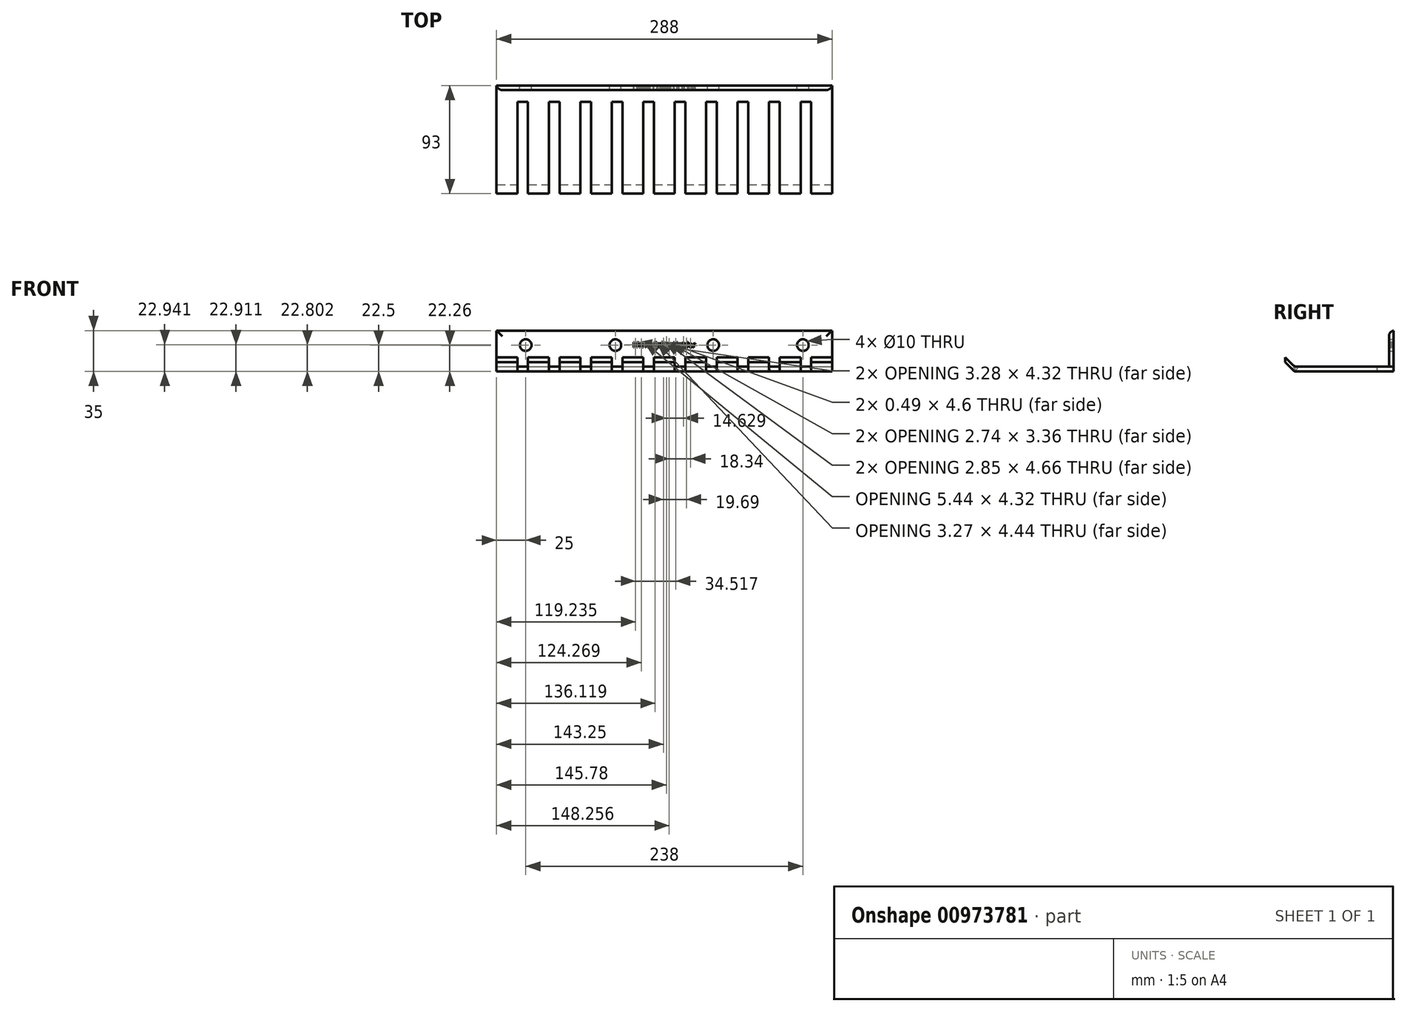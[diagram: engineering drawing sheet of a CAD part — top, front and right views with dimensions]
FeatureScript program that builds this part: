
annotation { "Feature Type Name" : "Feature", "Feature Type Description" : "" }
export const myFeature = defineFeature(function(context is Context, id is Id, definition is map)
    precondition{}
    {
        {
            var Q0;
            Q0=qCreatedBy(makeId("Front.planeOp"),FACE);
            var sketch = newSketch(context, id + "F0", { "sketchPlane" : qUnion([Q0])});
            skLineSegment(sketch, "E0", {"start": v(0, 0) * mm, "end": v(288, 0) * mm});
            skLineSegment(sketch, "E1", {"start": v(288, 0) * mm, "end": v(288, 35) * mm});
            skLineSegment(sketch, "E2", {"start": v(288, 35) * mm, "end": v(0, 35) * mm});
            skLineSegment(sketch, "E3", {"start": v(0, 35) * mm, "end": v(0, 0) * mm});
            skLineSegment(sketch, "E4", {"start": v(0, 22.5) * mm, "end": v(288, 22.5) * mm, "construction": true});
            skPoint(sketch, "E5", {"position": v(263, 22.5) * mm});
            skPoint(sketch, "E6", {"position": v(25, 22.5) * mm});
            skPoint(sketch, "E7", {"position": v(102, 22.5) * mm});
            skPoint(sketch, "E8", {"position": v(186, 22.5) * mm});
            skLineSegment(sketch, "E9", {"start": v(0, 4) * mm, "end": v(288, 4) * mm});
            skText(sketch, "E10", { "text": "HWM Cable Holder", "fontName": "OpenSans-Regular.ttf"});
            const initialGuessF0  = {"E10": [0.117, 0.02064, 1, 0, 0.00436]};
            skSetInitialGuess(sketch, initialGuessF0);
            skSolve(sketch);
        }
        {
            var Q0;
            {var subQ0=sQuery(id+"F0.wireOp",EDGE,"E2");Q0=makeQuery(id+"F0.imprint","IMPRINT",FACE,{"disambiguationData":[TD([[makeQuery(id+"F0.imprint","IMPRINT",EDGE,{"derivedFrom":subQ0}),1.0]])]});}
            extrude(context, id + "F1", {"entities" : qUnion([Q0]), "depth" : 4 * mm, "offsetDistance" : 25 * mm});
        }
        {
            var Q0;
            {var subQ0=sQuery(id+"F0.wireOp",EDGE,"E0");Q0=makeQuery(id+"F0.imprint","IMPRINT",FACE,{"disambiguationData":[TD([[makeQuery(id+"F0.imprint","IMPRINT",EDGE,{"derivedFrom":subQ0}),1.0]])]});}
            extrude(context, id + "F2", {"entities" : qUnion([Q0]), "depth" : 85 * mm, "offsetDistance" : 25 * mm});
        }
        {
            var Q0;
            Q0=sQuery(id+"F0.wireOp",VERTEX,"E6");
            var Q1;
            Q1=sQuery(id+"F0.wireOp",VERTEX,"E7");
            var Q2;
            Q2=sQuery(id+"F0.wireOp",VERTEX,"E8");
            var Q3;
            Q3=sQuery(id+"F0.wireOp",VERTEX,"E5");
            var Q4;
            Q4=makeQuery(id+"F1.opExtrude","SWEPT_BODY",BODY,{"disambiguationData":[OSD([sQuery(id+"F0.wireOp",EDGE,"E0"),sQuery(id+"F0.wireOp",EDGE,"E1"),sQuery(id+"F0.wireOp",EDGE,"E2"),sQuery(id+"F0.wireOp",EDGE,"E3")])]});
            hole(context, id + "F3", {"style" : HoleStyle.SIMPLE, "endStyle" : HoleEndStyle.THROUGH, "oppositeDirection" : true, "standardTappedOrClearance" : lookupTablePath({ "standard" : "ISO", "size" : "10", "type" : "Drilled" }), "standardBlindInLast" : lookupTablePath({ "standard" : "ISO", "size" : "10", "type" : "Drilled" }), "holeDiameter" : 10 * mm, "majorDiameter" : 6 * mm, "isTappedThrough" : true, "tappedDepth" : 12 * mm, "tapClearance" : 3, "locations" : qUnion([Q0, Q1, Q2, Q3]), "scope" : qUnion([Q4])});
        }
        {
            var Q0;
            Q0=makeQuery(id+"F2.opExtrude","SWEPT_FACE",FACE,{"disambiguationData":[OSD([sQuery(id+"F0.wireOp",EDGE,"E9")])]});
            var sketch = newSketch(context, id + "F4", { "sketchPlane" : qUnion([Q0])});
            skLineSegment(sketch, "E11", {"start": v(0, -14) * mm, "end": v(288, -14) * mm, "construction": true});
            skLineSegment(sketch, "E12", {"start": v(18, -85) * mm, "end": v(18, -14) * mm});
            skLineSegment(sketch, "E13", {"start": v(27, -85) * mm, "end": v(27, -14) * mm});
            skLineSegment(sketch, "E14", {"start": v(18, -85) * mm, "end": v(27, -85) * mm});
            skLineSegment(sketch, "E15", {"start": v(45, -14) * mm, "end": v(45, -85) * mm});
            skLineSegment(sketch, "E16", {"start": v(54, -14) * mm, "end": v(54, -85) * mm});
            skLineSegment(sketch, "E17", {"start": v(45, -85) * mm, "end": v(54, -85) * mm});
            skLineSegment(sketch, "E18", {"start": v(18, -14) * mm, "end": v(27, -14) * mm});
            skLineSegment(sketch, "E19", {"start": v(45, -14) * mm, "end": v(54, -14) * mm});
            skLineSegment(sketch, "E20", {"start": v(72, -14) * mm, "end": v(72, -85) * mm});
            skLineSegment(sketch, "E21", {"start": v(81, -14) * mm, "end": v(81, -85) * mm});
            skLineSegment(sketch, "E22", {"start": v(99, -14) * mm, "end": v(99, -85) * mm});
            skLineSegment(sketch, "E23", {"start": v(108, -14) * mm, "end": v(108, -85) * mm});
            skLineSegment(sketch, "E24", {"start": v(126, -14) * mm, "end": v(126, -85) * mm});
            skLineSegment(sketch, "E25", {"start": v(135, -14) * mm, "end": v(135, -85) * mm});
            skLineSegment(sketch, "E26", {"start": v(153, -14) * mm, "end": v(153, -85) * mm});
            skLineSegment(sketch, "E27", {"start": v(162, -14) * mm, "end": v(162, -85) * mm});
            skLineSegment(sketch, "E28", {"start": v(180, -14) * mm, "end": v(180, -85) * mm});
            skLineSegment(sketch, "E29", {"start": v(189, -14) * mm, "end": v(189, -85) * mm});
            skLineSegment(sketch, "E30", {"start": v(207, -14) * mm, "end": v(207, -85) * mm});
            skLineSegment(sketch, "E31", {"start": v(216, -14) * mm, "end": v(216, -85) * mm});
            skLineSegment(sketch, "E32", {"start": v(234, -14) * mm, "end": v(234, -85) * mm});
            skLineSegment(sketch, "E33", {"start": v(243, -14) * mm, "end": v(243, -85) * mm});
            skLineSegment(sketch, "E34", {"start": v(261, -14) * mm, "end": v(261, -85) * mm});
            skLineSegment(sketch, "E35", {"start": v(270, -14) * mm, "end": v(270, -85) * mm});
            skLineSegment(sketch, "E36", {"start": v(72, -14) * mm, "end": v(81, -14) * mm});
            skLineSegment(sketch, "E37", {"start": v(99, -14) * mm, "end": v(108, -14) * mm});
            skLineSegment(sketch, "E38", {"start": v(126, -14) * mm, "end": v(135, -14) * mm});
            skLineSegment(sketch, "E39", {"start": v(153, -14) * mm, "end": v(162, -14) * mm});
            skLineSegment(sketch, "E40", {"start": v(180, -14) * mm, "end": v(189, -14) * mm});
            skLineSegment(sketch, "E41", {"start": v(207, -14) * mm, "end": v(216, -14) * mm});
            skLineSegment(sketch, "E42", {"start": v(234, -14) * mm, "end": v(243, -14) * mm});
            skLineSegment(sketch, "E43", {"start": v(261, -14) * mm, "end": v(270, -14) * mm});
            skLineSegment(sketch, "E44", {"start": v(270, -85) * mm, "end": v(261, -85) * mm});
            skLineSegment(sketch, "E45", {"start": v(243, -85) * mm, "end": v(234, -85) * mm});
            skLineSegment(sketch, "E46", {"start": v(216, -85) * mm, "end": v(207, -85) * mm});
            skLineSegment(sketch, "E47", {"start": v(189, -85) * mm, "end": v(180, -85) * mm});
            skLineSegment(sketch, "E48", {"start": v(162, -85) * mm, "end": v(153, -85) * mm});
            skLineSegment(sketch, "E49", {"start": v(135, -85) * mm, "end": v(126, -85) * mm});
            skLineSegment(sketch, "E50", {"start": v(108, -85) * mm, "end": v(99, -85) * mm});
            skLineSegment(sketch, "E51", {"start": v(81, -85) * mm, "end": v(72, -85) * mm});
            skSolve(sketch);
        }
        {
            var Q0;
            Q0=makeQuery(id+"F2.opExtrude","CAP_FACE",FACE,{"disambiguationData":[OSD([sQuery(id+"F0.wireOp",EDGE,"E0"),sQuery(id+"F0.wireOp",EDGE,"E1"),sQuery(id+"F0.wireOp",EDGE,"E3"),sQuery(id+"F0.wireOp",EDGE,"E9")])],"isStart":false});
            var sketch = newSketch(context, id + "F5", { "sketchPlane" : qUnion([Q0])});
            skLineSegment(sketch, "E52", {"start": v(0, 4) * mm, "end": v(0, 0) * mm});
            skLineSegment(sketch, "E53", {"start": v(0, 0) * mm, "end": v(288, 0) * mm});
            skLineSegment(sketch, "E54", {"start": v(288, 0) * mm, "end": v(288, 4) * mm});
            skLineSegment(sketch, "E55", {"start": v(288, 4) * mm, "end": v(0, 4) * mm});
            skSolve(sketch);
        }
        {
            var Q0;
            Q0=makeQuery(id+"F5.imprint","IMPRINT",FACE,{"disambiguationData":[TD([[makeQuery(id+"F5.imprint","IMPRINT",EDGE,{"derivedFrom":sQuery(id+"F5.wireOp",EDGE,"E52")}),1.0]])]});
            extrude(context, id + "F6", {"entities" : qUnion([Q0]), "operationType" : NewBodyOperationType.ADD, "depth" : 8 * mm, "offsetDistance" : 25 * mm});
        }
        {
            var Q0;
            Q0=makeQuery(id+"F6.boolean.opBoolean","MERGE",FACE,{"derivedFrom":[makeQuery(id+"F2.opExtrude","SWEPT_FACE",FACE,{"disambiguationData":[OSD([sQuery(id+"F0.wireOp",EDGE,"E9")])]}),makeQuery(id+"F6.opExtrude","SWEPT_FACE",FACE,{"disambiguationData":[OSD([sQuery(id+"F5.wireOp",EDGE,"E55")])]})]});
            var sketch = newSketch(context, id + "F7", { "sketchPlane" : qUnion([Q0])});
            skLineSegment(sketch, "E56", {"start": v(0, -85.1) * mm, "end": v(288, -85.1) * mm});
            skLineSegment(sketch, "E57", {"start": v(288, -85.1) * mm, "end": v(288, -93) * mm});
            skLineSegment(sketch, "E58", {"start": v(288, -93) * mm, "end": v(0, -93) * mm});
            skLineSegment(sketch, "E59", {"start": v(0, -93) * mm, "end": v(0, -85.1) * mm});
            skSolve(sketch);
        }
        {
            var Q0;
            Q0=makeQuery(id+"F7.imprint","IMPRINT",FACE,{"disambiguationData":[TD([[makeQuery(id+"F7.imprint","IMPRINT",EDGE,{"derivedFrom":sQuery(id+"F7.wireOp",EDGE,"E56")}),-1.0]])]});
            extrude(context, id + "F8", {"entities" : qUnion([Q0]), "operationType" : NewBodyOperationType.ADD, "depth" : 8 * mm, "offsetDistance" : 25 * mm});
        }
        {
            var Q0;
            Q0=makeQuery(id+"F8.boolean.opBoolean","MERGE",FACE,{"derivedFrom":[makeQuery(id+"F6.boolean.opBoolean","MERGE",FACE,{"derivedFrom":[makeQuery(id+"F2.opExtrude","SWEPT_FACE",FACE,{"disambiguationData":[OSD([sQuery(id+"F0.wireOp",EDGE,"E1")])]}),makeQuery(id+"F6.opExtrude","SWEPT_FACE",FACE,{"disambiguationData":[OSD([sQuery(id+"F5.wireOp",EDGE,"E54")])]})]}),makeQuery(id+"F8.opExtrude","SWEPT_FACE",FACE,{"disambiguationData":[OSD([sQuery(id+"F7.wireOp",EDGE,"E57")])]})]});
            var sketch = newSketch(context, id + "F9", { "sketchPlane" : qUnion([Q0])});
            skLineSegment(sketch, "E60", {"start": v(-85.1, 4) * mm, "end": v(-85.1, 0) * mm, "construction": true});
            skLineSegment(sketch, "E61", {"start": v(-85.1, 4) * mm, "end": v(-93, 12) * mm});
            skLineSegment(sketch, "E62", {"start": v(-85.1, 0) * mm, "end": v(-93, 8) * mm});
            skLineSegment(sketch, "E63", {"start": v(-93, 8) * mm, "end": v(-93, 12) * mm});
            skLineSegment(sketch, "E64", {"start": v(-85.1, 4) * mm, "end": v(-85.1, 0) * mm});
            skSolve(sketch);
        }
        {
            var Q0;
            Q0=makeQuery(id+"F9.imprint","IMPRINT",FACE,{"disambiguationData":[TD([[makeQuery(id+"F9.imprint","IMPRINT",EDGE,{"derivedFrom":sQuery(id+"F9.wireOp",EDGE,"E61")}),-1.0]])]});
            var Q1;
            {var subQ0=sQuery(id+"F9.wireOp",EDGE,"E62");Q1=makeQuery(id+"F9.imprint","IMPRINT",FACE,{"disambiguationData":[TD([[makeQuery(id+"F9.imprint","IMPRINT",EDGE,{"derivedFrom":subQ0}),1.0]])]});}
            var Q2;
            Q2=makeQuery(id+"F8.boolean.opBoolean","MERGE",FACE,{"derivedFrom":[makeQuery(id+"F6.boolean.opBoolean","MERGE",FACE,{"derivedFrom":[makeQuery(id+"F2.opExtrude","SWEPT_FACE",FACE,{"disambiguationData":[OSD([sQuery(id+"F0.wireOp",EDGE,"E3")])]}),makeQuery(id+"F6.opExtrude","SWEPT_FACE",FACE,{"disambiguationData":[OSD([sQuery(id+"F5.wireOp",EDGE,"E52")])]})]}),makeQuery(id+"F8.opExtrude","SWEPT_FACE",FACE,{"disambiguationData":[OSD([sQuery(id+"F7.wireOp",EDGE,"E59")])]})]});
            extrude(context, id + "F10", {"entities" : qUnion([Q0, Q1]), "operationType" : NewBodyOperationType.REMOVE, "endBound" : BoundingType.UP_TO_SURFACE, "oppositeDirection" : true, "depth" : 25 * mm, "endBoundEntityFace" : qUnion([Q2]), "offsetDistance" : 25 * mm});
        }
        {
            var Q0;
            Q0=makeQuery(id+"F10.boolean.opBoolean","COPY",FACE,{"derivedFrom":makeQuery(id+"F10.opExtrude","SWEPT_FACE",FACE,{"disambiguationData":[OSD([sQuery(id+"F9.wireOp",EDGE,"E61")])]})});
            var sketch = newSketch(context, id + "F11", { "sketchPlane" : qUnion([Q0])});
            skLineSegment(sketch, "E65", {"start": v(-18, 62.64) * mm, "end": v(-18, 73.89) * mm});
            skLineSegment(sketch, "E66", {"start": v(-27, 62.64) * mm, "end": v(-27, 73.89) * mm});
            skLineSegment(sketch, "E67", {"start": v(-45, 62.64) * mm, "end": v(-45, 73.89) * mm});
            skLineSegment(sketch, "E68", {"start": v(-54, 62.64) * mm, "end": v(-54, 73.89) * mm});
            skLineSegment(sketch, "E69", {"start": v(-72, 62.64) * mm, "end": v(-72, 73.89) * mm});
            skLineSegment(sketch, "E70", {"start": v(-81, 62.64) * mm, "end": v(-81, 73.89) * mm});
            skLineSegment(sketch, "E71", {"start": v(-99, 62.64) * mm, "end": v(-99, 73.89) * mm});
            skLineSegment(sketch, "E72", {"start": v(-108, 62.64) * mm, "end": v(-108, 73.89) * mm});
            skLineSegment(sketch, "E73", {"start": v(-126, 62.64) * mm, "end": v(-126, 73.89) * mm});
            skLineSegment(sketch, "E74", {"start": v(-135, 62.64) * mm, "end": v(-135, 73.89) * mm});
            skLineSegment(sketch, "E75", {"start": v(-153, 62.64) * mm, "end": v(-153, 73.89) * mm});
            skLineSegment(sketch, "E76", {"start": v(-162, 62.64) * mm, "end": v(-162, 73.89) * mm});
            skLineSegment(sketch, "E77", {"start": v(-180, 62.64) * mm, "end": v(-180, 73.89) * mm});
            skLineSegment(sketch, "E78", {"start": v(-189, 62.64) * mm, "end": v(-189, 73.89) * mm});
            skLineSegment(sketch, "E79", {"start": v(-207, 62.64) * mm, "end": v(-207, 73.89) * mm});
            skLineSegment(sketch, "E80", {"start": v(-216, 62.64) * mm, "end": v(-216, 73.89) * mm});
            skLineSegment(sketch, "E81", {"start": v(-234, 62.64) * mm, "end": v(-234, 73.89) * mm});
            skLineSegment(sketch, "E82", {"start": v(-243, 62.64) * mm, "end": v(-243, 73.89) * mm});
            skLineSegment(sketch, "E83", {"start": v(-261, 62.64) * mm, "end": v(-261, 73.89) * mm});
            skLineSegment(sketch, "E84", {"start": v(-270, 62.64) * mm, "end": v(-270, 73.89) * mm});
            skSolve(sketch);
        }
        {
            var Q0;
            Q0=makeQuery(id+"F4.imprint","IMPRINT",FACE,{"disambiguationData":[TD([[makeQuery(id+"F4.imprint","IMPRINT",EDGE,{"derivedFrom":sQuery(id+"F4.wireOp",EDGE,"E12")}),-1.0]])]});
            var Q1;
            Q1=makeQuery(id+"F4.imprint","IMPRINT",FACE,{"disambiguationData":[TD([[makeQuery(id+"F4.imprint","IMPRINT",EDGE,{"derivedFrom":sQuery(id+"F4.wireOp",EDGE,"E15")}),1.0]])]});
            var Q2;
            Q2=makeQuery(id+"F4.imprint","IMPRINT",FACE,{"disambiguationData":[TD([[makeQuery(id+"F4.imprint","IMPRINT",EDGE,{"derivedFrom":sQuery(id+"F4.wireOp",EDGE,"E20")}),1.0]])]});
            var Q3;
            Q3=makeQuery(id+"F4.imprint","IMPRINT",FACE,{"disambiguationData":[TD([[makeQuery(id+"F4.imprint","IMPRINT",EDGE,{"derivedFrom":sQuery(id+"F4.wireOp",EDGE,"E22")}),1.0]])]});
            var Q4;
            Q4=makeQuery(id+"F4.imprint","IMPRINT",FACE,{"disambiguationData":[TD([[makeQuery(id+"F4.imprint","IMPRINT",EDGE,{"derivedFrom":sQuery(id+"F4.wireOp",EDGE,"E24")}),1.0]])]});
            var Q5;
            Q5=makeQuery(id+"F4.imprint","IMPRINT",FACE,{"disambiguationData":[TD([[makeQuery(id+"F4.imprint","IMPRINT",EDGE,{"derivedFrom":sQuery(id+"F4.wireOp",EDGE,"E26")}),1.0]])]});
            var Q6;
            Q6=makeQuery(id+"F4.imprint","IMPRINT",FACE,{"disambiguationData":[TD([[makeQuery(id+"F4.imprint","IMPRINT",EDGE,{"derivedFrom":sQuery(id+"F4.wireOp",EDGE,"E28")}),1.0]])]});
            var Q7;
            Q7=makeQuery(id+"F4.imprint","IMPRINT",FACE,{"disambiguationData":[TD([[makeQuery(id+"F4.imprint","IMPRINT",EDGE,{"derivedFrom":sQuery(id+"F4.wireOp",EDGE,"E30")}),1.0]])]});
            var Q8;
            Q8=makeQuery(id+"F4.imprint","IMPRINT",FACE,{"disambiguationData":[TD([[makeQuery(id+"F4.imprint","IMPRINT",EDGE,{"derivedFrom":sQuery(id+"F4.wireOp",EDGE,"E32")}),1.0]])]});
            var Q9;
            Q9=makeQuery(id+"F4.imprint","IMPRINT",FACE,{"disambiguationData":[TD([[makeQuery(id+"F4.imprint","IMPRINT",EDGE,{"derivedFrom":sQuery(id+"F4.wireOp",EDGE,"E34")}),1.0]])]});
            var Q10;
            Q10=makeQuery(id+"F6.boolean.opBoolean","MERGE",FACE,{"derivedFrom":[makeQuery(id+"F2.opExtrude","SWEPT_FACE",FACE,{"disambiguationData":[OSD([sQuery(id+"F0.wireOp",EDGE,"E0")])]}),makeQuery(id+"F6.opExtrude","SWEPT_FACE",FACE,{"disambiguationData":[OSD([sQuery(id+"F5.wireOp",EDGE,"E53")])]})]});
            extrude(context, id + "F12", {"entities" : qUnion([Q0, Q1, Q2, Q3, Q4, Q5, Q6, Q7, Q8, Q9]), "operationType" : NewBodyOperationType.REMOVE, "endBound" : BoundingType.UP_TO_SURFACE, "oppositeDirection" : true, "depth" : 4 * mm, "endBoundEntityFace" : qUnion([Q10]), "offsetDistance" : 25 * mm});
        }
        {
            var Q0;
            {var subQ0=sQuery(id+"F11.wireOp",EDGE,"E83");Q0=makeQuery(id+"F11.imprint","IMPRINT",FACE,{"disambiguationData":[TD([[makeQuery(id+"F11.imprint","IMPRINT",EDGE,{"derivedFrom":subQ0}),1.0]])]});}
            var Q1;
            {var subQ0=sQuery(id+"F11.wireOp",EDGE,"E81");Q1=makeQuery(id+"F11.imprint","IMPRINT",FACE,{"disambiguationData":[TD([[makeQuery(id+"F11.imprint","IMPRINT",EDGE,{"derivedFrom":subQ0}),1.0]])]});}
            var Q2;
            {var subQ0=sQuery(id+"F11.wireOp",EDGE,"E79");Q2=makeQuery(id+"F11.imprint","IMPRINT",FACE,{"disambiguationData":[TD([[makeQuery(id+"F11.imprint","IMPRINT",EDGE,{"derivedFrom":subQ0}),1.0]])]});}
            var Q3;
            {var subQ0=sQuery(id+"F11.wireOp",EDGE,"E77");Q3=makeQuery(id+"F11.imprint","IMPRINT",FACE,{"disambiguationData":[TD([[makeQuery(id+"F11.imprint","IMPRINT",EDGE,{"derivedFrom":subQ0}),1.0]])]});}
            var Q4;
            {var subQ0=sQuery(id+"F11.wireOp",EDGE,"E75");Q4=makeQuery(id+"F11.imprint","IMPRINT",FACE,{"disambiguationData":[TD([[makeQuery(id+"F11.imprint","IMPRINT",EDGE,{"derivedFrom":subQ0}),1.0]])]});}
            var Q5;
            {var subQ0=sQuery(id+"F11.wireOp",EDGE,"E73");Q5=makeQuery(id+"F11.imprint","IMPRINT",FACE,{"disambiguationData":[TD([[makeQuery(id+"F11.imprint","IMPRINT",EDGE,{"derivedFrom":subQ0}),1.0]])]});}
            var Q6;
            {var subQ0=sQuery(id+"F11.wireOp",EDGE,"E71");Q6=makeQuery(id+"F11.imprint","IMPRINT",FACE,{"disambiguationData":[TD([[makeQuery(id+"F11.imprint","IMPRINT",EDGE,{"derivedFrom":subQ0}),1.0]])]});}
            var Q7;
            {var subQ0=sQuery(id+"F11.wireOp",EDGE,"E69");Q7=makeQuery(id+"F11.imprint","IMPRINT",FACE,{"disambiguationData":[TD([[makeQuery(id+"F11.imprint","IMPRINT",EDGE,{"derivedFrom":subQ0}),1.0]])]});}
            var Q8;
            {var subQ0=sQuery(id+"F11.wireOp",EDGE,"E67");Q8=makeQuery(id+"F11.imprint","IMPRINT",FACE,{"disambiguationData":[TD([[makeQuery(id+"F11.imprint","IMPRINT",EDGE,{"derivedFrom":subQ0}),1.0]])]});}
            var Q9;
            {var subQ0=sQuery(id+"F11.wireOp",EDGE,"E65");Q9=makeQuery(id+"F11.imprint","IMPRINT",FACE,{"disambiguationData":[TD([[makeQuery(id+"F11.imprint","IMPRINT",EDGE,{"derivedFrom":subQ0}),1.0]])]});}
            var Q10;
            Q10=makeQuery(id+"F10.boolean.opBoolean","COPY",FACE,{"derivedFrom":makeQuery(id+"F10.opExtrude","SWEPT_FACE",FACE,{"disambiguationData":[OSD([sQuery(id+"F9.wireOp",EDGE,"E62")])]})});
            var Q11;
            Q11=makeQuery(id+"F10.boolean.opBoolean","COPY",FACE,{"derivedFrom":makeQuery(id+"F10.opExtrude","SWEPT_FACE",FACE,{"disambiguationData":[OSD([sQuery(id+"F9.wireOp",EDGE,"E62")])]})});
            extrude(context, id + "F13", {"entities" : qUnion([Q0, Q1, Q2, Q3, Q4, Q5, Q6, Q7, Q8, Q9, Q10]), "operationType" : NewBodyOperationType.REMOVE, "oppositeDirection" : true, "depth" : 4 * mm, "endBoundEntityFace" : qUnion([Q11]), "offsetDistance" : 25 * mm});
        }
        {
            var Q0;
            Q0=makeQuery(id+"F10.boolean.opBoolean","COPY",FACE,{"derivedFrom":makeQuery(id+"F10.opExtrude","SWEPT_FACE",FACE,{"disambiguationData":[OSD([sQuery(id+"F9.wireOp",EDGE,"E62")])]})});
            var sketch = newSketch(context, id + "F14", { "sketchPlane" : qUnion([Q0])});
            skLineSegment(sketch, "E85", {"start": v(180, 62.64) * mm, "end": v(180, 59.8) * mm});
            skLineSegment(sketch, "E86", {"start": v(180, 59.8) * mm, "end": v(189, 59.8) * mm});
            skLineSegment(sketch, "E87", {"start": v(189, 59.8) * mm, "end": v(189, 62.64) * mm});
            skLineSegment(sketch, "E88", {"start": v(189, 62.64) * mm, "end": v(180, 62.64) * mm});
            skLineSegment(sketch, "E89", {"start": v(261, 62.64) * mm, "end": v(270, 62.64) * mm});
            skLineSegment(sketch, "E90", {"start": v(270, 62.64) * mm, "end": v(270, 59.8) * mm});
            skLineSegment(sketch, "E91", {"start": v(270, 59.8) * mm, "end": v(261, 59.8) * mm});
            skLineSegment(sketch, "E92", {"start": v(261, 59.8) * mm, "end": v(261, 62.64) * mm});
            skLineSegment(sketch, "E93", {"start": v(243, 62.64) * mm, "end": v(243, 59.8) * mm});
            skLineSegment(sketch, "E94", {"start": v(243, 59.8) * mm, "end": v(234.03, 59.8) * mm});
            skLineSegment(sketch, "E95", {"start": v(234.03, 59.8) * mm, "end": v(234, 62.64) * mm});
            skLineSegment(sketch, "E96", {"start": v(234, 62.64) * mm, "end": v(243, 62.64) * mm});
            skLineSegment(sketch, "E97", {"start": v(216, 62.64) * mm, "end": v(207, 62.64) * mm});
            skLineSegment(sketch, "E98", {"start": v(207, 62.64) * mm, "end": v(207, 59.8) * mm});
            skLineSegment(sketch, "E99", {"start": v(207, 59.8) * mm, "end": v(216, 59.8) * mm});
            skLineSegment(sketch, "E100", {"start": v(216, 59.8) * mm, "end": v(216, 62.64) * mm});
            skLineSegment(sketch, "E101", {"start": v(162, 62.64) * mm, "end": v(162, 59.8) * mm});
            skLineSegment(sketch, "E102", {"start": v(162, 59.8) * mm, "end": v(152.94, 59.8) * mm});
            skLineSegment(sketch, "E103", {"start": v(152.94, 59.8) * mm, "end": v(153, 62.64) * mm});
            skLineSegment(sketch, "E104", {"start": v(153, 62.64) * mm, "end": v(162, 62.64) * mm});
            skLineSegment(sketch, "E105", {"start": v(126, 62.64) * mm, "end": v(135, 62.64) * mm});
            skLineSegment(sketch, "E106", {"start": v(135, 62.64) * mm, "end": v(135, 59.8) * mm});
            skLineSegment(sketch, "E107", {"start": v(135, 59.8) * mm, "end": v(126, 59.8) * mm});
            skLineSegment(sketch, "E108", {"start": v(126, 59.8) * mm, "end": v(126, 62.64) * mm});
            skLineSegment(sketch, "E109", {"start": v(108, 62.64) * mm, "end": v(99, 62.64) * mm});
            skLineSegment(sketch, "E110", {"start": v(99, 62.64) * mm, "end": v(99, 59.8) * mm});
            skLineSegment(sketch, "E111", {"start": v(99, 59.8) * mm, "end": v(108, 59.8) * mm});
            skLineSegment(sketch, "E112", {"start": v(108, 59.8) * mm, "end": v(108, 62.64) * mm});
            skLineSegment(sketch, "E113", {"start": v(81, 62.64) * mm, "end": v(72, 62.64) * mm});
            skLineSegment(sketch, "E114", {"start": v(72, 62.64) * mm, "end": v(72, 59.8) * mm});
            skLineSegment(sketch, "E115", {"start": v(72, 59.8) * mm, "end": v(81, 59.8) * mm});
            skLineSegment(sketch, "E116", {"start": v(81, 59.8) * mm, "end": v(81, 62.64) * mm});
            skLineSegment(sketch, "E117", {"start": v(54, 62.64) * mm, "end": v(45, 62.64) * mm});
            skLineSegment(sketch, "E118", {"start": v(45, 62.64) * mm, "end": v(45, 59.8) * mm});
            skLineSegment(sketch, "E119", {"start": v(45, 59.8) * mm, "end": v(54, 59.8) * mm});
            skLineSegment(sketch, "E120", {"start": v(54, 59.8) * mm, "end": v(54, 62.64) * mm});
            skLineSegment(sketch, "E121", {"start": v(27, 62.64) * mm, "end": v(18, 62.64) * mm});
            skLineSegment(sketch, "E122", {"start": v(18, 62.64) * mm, "end": v(18, 59.8) * mm});
            skLineSegment(sketch, "E123", {"start": v(18, 59.8) * mm, "end": v(27, 59.8) * mm});
            skLineSegment(sketch, "E124", {"start": v(27, 59.8) * mm, "end": v(27, 62.64) * mm});
            skSolve(sketch);
        }
        {
            var Q0;
            Q0=makeQuery(id+"F14.imprint","IMPRINT",FACE,{"disambiguationData":[TD([[makeQuery(id+"F14.imprint","IMPRINT",EDGE,{"derivedFrom":sQuery(id+"F14.wireOp",EDGE,"E85")}),1.0]])]});
            extrude(context, id + "F15", {"entities" : qUnion([Q0]), "operationType" : NewBodyOperationType.REMOVE, "oppositeDirection" : true, "depth" : 4 * mm, "offsetDistance" : 25 * mm});
        }
        {
            var Q0;
            Q0 = qSketchRegion(id + "F14", true);
            extrude(context, id + "F16", {"entities" : qUnion([Q0]), "operationType" : NewBodyOperationType.REMOVE, "oppositeDirection" : true, "depth" : 4 * mm, "offsetDistance" : 25 * mm});
        }
        {
            var Q0;
            Q0=makeQuery(id+"F6.boolean.opBoolean","MERGE",FACE,{"derivedFrom":[makeQuery(id+"F2.opExtrude","SWEPT_FACE",FACE,{"disambiguationData":[OSD([sQuery(id+"F0.wireOp",EDGE,"E0")])]}),makeQuery(id+"F6.opExtrude","SWEPT_FACE",FACE,{"disambiguationData":[OSD([sQuery(id+"F5.wireOp",EDGE,"E53")])]})]});
            var sketch = newSketch(context, id + "F17", { "sketchPlane" : qUnion([Q0])});
            skLineSegment(sketch, "E125", {"start": v(270, 85.1) * mm, "end": v(270, 85) * mm});
            skLineSegment(sketch, "E126", {"start": v(270, 85) * mm, "end": v(261, 85) * mm});
            skLineSegment(sketch, "E127", {"start": v(261, 85) * mm, "end": v(261, 85.1) * mm});
            skLineSegment(sketch, "E128", {"start": v(261, 85.1) * mm, "end": v(270, 85.1) * mm});
            skLineSegment(sketch, "E129", {"start": v(243, 85.1) * mm, "end": v(243, 85) * mm});
            skLineSegment(sketch, "E130", {"start": v(243, 85) * mm, "end": v(234, 85) * mm});
            skLineSegment(sketch, "E131", {"start": v(234, 85) * mm, "end": v(234.03, 85.1) * mm});
            skLineSegment(sketch, "E132", {"start": v(234.03, 85.1) * mm, "end": v(243, 85.1) * mm});
            skLineSegment(sketch, "E133", {"start": v(216, 85.1) * mm, "end": v(216, 85) * mm});
            skLineSegment(sketch, "E134", {"start": v(216, 85) * mm, "end": v(207, 85) * mm});
            skLineSegment(sketch, "E135", {"start": v(207, 85) * mm, "end": v(207, 85.1) * mm});
            skLineSegment(sketch, "E136", {"start": v(207, 85.1) * mm, "end": v(216, 85.1) * mm});
            skLineSegment(sketch, "E137", {"start": v(189, 85.1) * mm, "end": v(189, 85) * mm});
            skLineSegment(sketch, "E138", {"start": v(189, 85) * mm, "end": v(180, 85) * mm});
            skLineSegment(sketch, "E139", {"start": v(180, 85) * mm, "end": v(180, 85.1) * mm});
            skLineSegment(sketch, "E140", {"start": v(180, 85.1) * mm, "end": v(189, 85.1) * mm});
            skLineSegment(sketch, "E141", {"start": v(162, 85.1) * mm, "end": v(162, 85) * mm});
            skLineSegment(sketch, "E142", {"start": v(162, 85) * mm, "end": v(153, 85) * mm});
            skLineSegment(sketch, "E143", {"start": v(153, 85) * mm, "end": v(152.94, 85.1) * mm});
            skLineSegment(sketch, "E144", {"start": v(152.94, 85.1) * mm, "end": v(162, 85.1) * mm});
            skLineSegment(sketch, "E145", {"start": v(135, 85.1) * mm, "end": v(135, 85) * mm});
            skLineSegment(sketch, "E146", {"start": v(135, 85) * mm, "end": v(126, 85) * mm});
            skLineSegment(sketch, "E147", {"start": v(126, 85) * mm, "end": v(126, 85.1) * mm});
            skLineSegment(sketch, "E148", {"start": v(126, 85.1) * mm, "end": v(135, 85.1) * mm});
            skLineSegment(sketch, "E149", {"start": v(108, 85.1) * mm, "end": v(108, 85) * mm});
            skLineSegment(sketch, "E150", {"start": v(108, 85) * mm, "end": v(99, 85) * mm});
            skLineSegment(sketch, "E151", {"start": v(99, 85) * mm, "end": v(99, 85.1) * mm});
            skLineSegment(sketch, "E152", {"start": v(99, 85.1) * mm, "end": v(108, 85.1) * mm});
            skLineSegment(sketch, "E153", {"start": v(81, 85.1) * mm, "end": v(81, 85) * mm});
            skLineSegment(sketch, "E154", {"start": v(81, 85) * mm, "end": v(72, 85) * mm});
            skLineSegment(sketch, "E155", {"start": v(72, 85) * mm, "end": v(72, 85.1) * mm});
            skLineSegment(sketch, "E156", {"start": v(72, 85.1) * mm, "end": v(81, 85.1) * mm});
            skLineSegment(sketch, "E157", {"start": v(54, 85.1) * mm, "end": v(54, 85) * mm});
            skLineSegment(sketch, "E158", {"start": v(54, 85) * mm, "end": v(45, 85) * mm});
            skLineSegment(sketch, "E159", {"start": v(45, 85) * mm, "end": v(45, 85.1) * mm});
            skLineSegment(sketch, "E160", {"start": v(45, 85.1) * mm, "end": v(54, 85.1) * mm});
            skLineSegment(sketch, "E161", {"start": v(27, 85.1) * mm, "end": v(27, 85) * mm});
            skLineSegment(sketch, "E162", {"start": v(27, 85) * mm, "end": v(18, 85) * mm});
            skLineSegment(sketch, "E163", {"start": v(18, 85) * mm, "end": v(18, 85.1) * mm});
            skLineSegment(sketch, "E164", {"start": v(18, 85.1) * mm, "end": v(27, 85.1) * mm});
            skSolve(sketch);
        }
        {
            var Q0;
            Q0 = qSketchRegion(id + "F17", true);
            extrude(context, id + "F18", {"entities" : qUnion([Q0]), "operationType" : NewBodyOperationType.REMOVE, "endBound" : BoundingType.UP_TO_NEXT, "oppositeDirection" : true, "depth" : 25 * mm, "offsetDistance" : 25 * mm});
        }
        {
            var Q0;
            {var subQ0=sQuery(id+"F11.wireOp",EDGE,"E72");var subQ1=sQuery(id+"F9.wireOp",EDGE,"E61");var subQ3=sQuery(id+"F9.wireOp",EDGE,"E64");var subQ4=sQuery(id+"F7.wireOp",EDGE,"E57");var subQ5=sQuery(id+"F7.wireOp",EDGE,"E56");var subQ6=sQuery(id+"F5.wireOp",EDGE,"E55");var subQ7=sQuery(id+"F5.wireOp",EDGE,"E54");var subQ8=sQuery(id+"F0.wireOp",EDGE,"E9");var subQ9=sQuery(id+"F0.wireOp",EDGE,"E1");var subQ10=makeQuery(id+"F10.boolean.opBoolean","MERGE",EDGE,{"derivedFrom":[makeQuery(id+"F8.opExtrude","CAP_EDGE",EDGE,{"disambiguationData":[OSD([subQ5])],"isStart":true})],"fromTools":[makeQuery(id+"F10.opExtrude","SWEPT_EDGE",EDGE,{"disambiguationData":[OSD([subQ9,subQ8,subQ7,subQ6,subQ5,subQ4,subQ1,subQ3])]})]});Q0=makeQuery(id+"F13.boolean.opBoolean","SPLIT",EDGE,{"disambiguationData":[TD([makeQuery(id+"F13.opExtrude","SWEPT_FACE",FACE,{"disambiguationData":[OSD([subQ0])]})])],"derivedFrom":subQ10});}
            var Q1;
            {var subQ0=sQuery(id+"F11.wireOp",EDGE,"E70");var subQ1=sQuery(id+"F0.wireOp",EDGE,"E9");var subQ2=sQuery(id+"F9.wireOp",EDGE,"E61");var subQ3=sQuery(id+"F5.wireOp",EDGE,"E55");var subQ5=sQuery(id+"F9.wireOp",EDGE,"E64");var subQ6=sQuery(id+"F7.wireOp",EDGE,"E57");var subQ7=sQuery(id+"F7.wireOp",EDGE,"E56");var subQ8=sQuery(id+"F5.wireOp",EDGE,"E54");var subQ9=sQuery(id+"F0.wireOp",EDGE,"E1");var subQ10=makeQuery(id+"F10.boolean.opBoolean","MERGE",EDGE,{"derivedFrom":[makeQuery(id+"F8.opExtrude","CAP_EDGE",EDGE,{"disambiguationData":[OSD([subQ7])],"isStart":true})],"fromTools":[makeQuery(id+"F10.opExtrude","SWEPT_EDGE",EDGE,{"disambiguationData":[OSD([subQ9,subQ1,subQ8,subQ3,subQ7,subQ6,subQ2,subQ5])]})]});Q1=makeQuery(id+"F13.boolean.opBoolean","SPLIT",EDGE,{"disambiguationData":[TD([makeQuery(id+"F13.opExtrude","SWEPT_FACE",FACE,{"disambiguationData":[OSD([subQ0])]})])],"derivedFrom":subQ10});}
            var Q2;
            {var subQ0=sQuery(id+"F11.wireOp",EDGE,"E68");var subQ1=sQuery(id+"F9.wireOp",EDGE,"E64");var subQ2=sQuery(id+"F9.wireOp",EDGE,"E61");var subQ3=sQuery(id+"F7.wireOp",EDGE,"E57");var subQ4=sQuery(id+"F7.wireOp",EDGE,"E56");var subQ5=sQuery(id+"F5.wireOp",EDGE,"E55");var subQ6=sQuery(id+"F5.wireOp",EDGE,"E54");var subQ7=sQuery(id+"F0.wireOp",EDGE,"E9");var subQ8=sQuery(id+"F0.wireOp",EDGE,"E1");var subQ9=makeQuery(id+"F10.boolean.opBoolean","MERGE",EDGE,{"derivedFrom":[makeQuery(id+"F8.opExtrude","CAP_EDGE",EDGE,{"disambiguationData":[OSD([subQ4])],"isStart":true})],"fromTools":[makeQuery(id+"F10.opExtrude","SWEPT_EDGE",EDGE,{"disambiguationData":[OSD([subQ8,subQ7,subQ6,subQ5,subQ4,subQ3,subQ2,subQ1])]})]});Q2=makeQuery(id+"F13.boolean.opBoolean","SPLIT",EDGE,{"disambiguationData":[TD([makeQuery(id+"F13.opExtrude","SWEPT_FACE",FACE,{"disambiguationData":[OSD([subQ0])]})])],"derivedFrom":subQ9});}
            var Q3;
            {var subQ0=sQuery(id+"F9.wireOp",EDGE,"E61");var subQ1=sQuery(id+"F11.wireOp",EDGE,"E66");var subQ2=sQuery(id+"F5.wireOp",EDGE,"E55");var subQ3=sQuery(id+"F0.wireOp",EDGE,"E9");var subQ5=sQuery(id+"F9.wireOp",EDGE,"E64");var subQ6=sQuery(id+"F7.wireOp",EDGE,"E57");var subQ7=sQuery(id+"F7.wireOp",EDGE,"E56");var subQ8=sQuery(id+"F5.wireOp",EDGE,"E54");var subQ9=sQuery(id+"F0.wireOp",EDGE,"E1");var subQ10=makeQuery(id+"F10.boolean.opBoolean","MERGE",EDGE,{"derivedFrom":[makeQuery(id+"F8.opExtrude","CAP_EDGE",EDGE,{"disambiguationData":[OSD([subQ7])],"isStart":true})],"fromTools":[makeQuery(id+"F10.opExtrude","SWEPT_EDGE",EDGE,{"disambiguationData":[OSD([subQ9,subQ3,subQ8,subQ2,subQ7,subQ6,subQ0,subQ5])]})]});Q3=makeQuery(id+"F13.boolean.opBoolean","SPLIT",EDGE,{"disambiguationData":[TD([makeQuery(id+"F13.opExtrude","SWEPT_FACE",FACE,{"disambiguationData":[OSD([subQ1])]})])],"derivedFrom":subQ10});}
            var Q4;
            {var subQ0=sQuery(id+"F5.wireOp",EDGE,"E55");var subQ1=sQuery(id+"F0.wireOp",EDGE,"E9");var subQ3=sQuery(id+"F9.wireOp",EDGE,"E61");var subQ4=sQuery(id+"F9.wireOp",EDGE,"E64");var subQ5=sQuery(id+"F7.wireOp",EDGE,"E57");var subQ6=sQuery(id+"F7.wireOp",EDGE,"E56");var subQ7=sQuery(id+"F5.wireOp",EDGE,"E54");var subQ8=sQuery(id+"F0.wireOp",EDGE,"E1");var subQ9=makeQuery(id+"F10.boolean.opBoolean","MERGE",EDGE,{"derivedFrom":[makeQuery(id+"F8.opExtrude","CAP_EDGE",EDGE,{"disambiguationData":[OSD([subQ6])],"isStart":true})],"fromTools":[makeQuery(id+"F10.opExtrude","SWEPT_EDGE",EDGE,{"disambiguationData":[OSD([subQ8,subQ1,subQ7,subQ0,subQ6,subQ5,subQ3,subQ4])]})]});Q4=makeQuery(id+"F13.boolean.opBoolean","SPLIT",EDGE,{"disambiguationData":[TD([makeQuery(id+"F2.opExtrude","SWEPT_FACE",FACE,{"disambiguationData":[OSD([sQuery(id+"F0.wireOp",EDGE,"E3")])]})])],"derivedFrom":subQ9});}
            var Q5;
            {var subQ0=sQuery(id+"F11.wireOp",EDGE,"E74");var subQ1=sQuery(id+"F9.wireOp",EDGE,"E61");var subQ2=sQuery(id+"F9.wireOp",EDGE,"E64");var subQ3=sQuery(id+"F7.wireOp",EDGE,"E57");var subQ4=sQuery(id+"F7.wireOp",EDGE,"E56");var subQ5=sQuery(id+"F5.wireOp",EDGE,"E55");var subQ6=sQuery(id+"F5.wireOp",EDGE,"E54");var subQ7=sQuery(id+"F0.wireOp",EDGE,"E9");var subQ8=sQuery(id+"F0.wireOp",EDGE,"E1");var subQ9=makeQuery(id+"F10.boolean.opBoolean","MERGE",EDGE,{"derivedFrom":[makeQuery(id+"F8.opExtrude","CAP_EDGE",EDGE,{"disambiguationData":[OSD([subQ4])],"isStart":true})],"fromTools":[makeQuery(id+"F10.opExtrude","SWEPT_EDGE",EDGE,{"disambiguationData":[OSD([subQ8,subQ7,subQ6,subQ5,subQ4,subQ3,subQ1,subQ2])]})]});Q5=makeQuery(id+"F13.boolean.opBoolean","SPLIT",EDGE,{"disambiguationData":[TD([makeQuery(id+"F13.opExtrude","SWEPT_FACE",FACE,{"disambiguationData":[OSD([subQ0])]})])],"derivedFrom":subQ9});}
            var Q6;
            {var subQ0=sQuery(id+"F9.wireOp",EDGE,"E61");var subQ1=sQuery(id+"F11.wireOp",EDGE,"E76");var subQ2=sQuery(id+"F5.wireOp",EDGE,"E55");var subQ4=sQuery(id+"F9.wireOp",EDGE,"E64");var subQ5=sQuery(id+"F7.wireOp",EDGE,"E57");var subQ6=sQuery(id+"F7.wireOp",EDGE,"E56");var subQ7=sQuery(id+"F5.wireOp",EDGE,"E54");var subQ8=sQuery(id+"F0.wireOp",EDGE,"E9");var subQ9=sQuery(id+"F0.wireOp",EDGE,"E1");var subQ10=makeQuery(id+"F10.boolean.opBoolean","MERGE",EDGE,{"derivedFrom":[makeQuery(id+"F8.opExtrude","CAP_EDGE",EDGE,{"disambiguationData":[OSD([subQ6])],"isStart":true})],"fromTools":[makeQuery(id+"F10.opExtrude","SWEPT_EDGE",EDGE,{"disambiguationData":[OSD([subQ9,subQ8,subQ7,subQ2,subQ6,subQ5,subQ0,subQ4])]})]});Q6=makeQuery(id+"F13.boolean.opBoolean","SPLIT",EDGE,{"disambiguationData":[TD([makeQuery(id+"F13.opExtrude","SWEPT_FACE",FACE,{"disambiguationData":[OSD([subQ1])]})])],"derivedFrom":subQ10});}
            var Q7;
            {var subQ0=sQuery(id+"F11.wireOp",EDGE,"E78");var subQ1=sQuery(id+"F9.wireOp",EDGE,"E61");var subQ2=sQuery(id+"F5.wireOp",EDGE,"E55");var subQ3=sQuery(id+"F9.wireOp",EDGE,"E64");var subQ4=sQuery(id+"F7.wireOp",EDGE,"E57");var subQ5=sQuery(id+"F7.wireOp",EDGE,"E56");var subQ6=sQuery(id+"F5.wireOp",EDGE,"E54");var subQ7=sQuery(id+"F0.wireOp",EDGE,"E9");var subQ8=sQuery(id+"F0.wireOp",EDGE,"E1");var subQ9=makeQuery(id+"F10.boolean.opBoolean","MERGE",EDGE,{"derivedFrom":[makeQuery(id+"F8.opExtrude","CAP_EDGE",EDGE,{"disambiguationData":[OSD([subQ5])],"isStart":true})],"fromTools":[makeQuery(id+"F10.opExtrude","SWEPT_EDGE",EDGE,{"disambiguationData":[OSD([subQ8,subQ7,subQ6,subQ2,subQ5,subQ4,subQ1,subQ3])]})]});Q7=makeQuery(id+"F13.boolean.opBoolean","SPLIT",EDGE,{"disambiguationData":[TD([makeQuery(id+"F13.opExtrude","SWEPT_FACE",FACE,{"disambiguationData":[OSD([subQ0])]})])],"derivedFrom":subQ9});}
            var Q8;
            {var subQ0=sQuery(id+"F11.wireOp",EDGE,"E80");var subQ1=sQuery(id+"F9.wireOp",EDGE,"E61");var subQ3=sQuery(id+"F5.wireOp",EDGE,"E55");var subQ4=sQuery(id+"F0.wireOp",EDGE,"E9");var subQ5=sQuery(id+"F9.wireOp",EDGE,"E64");var subQ6=sQuery(id+"F7.wireOp",EDGE,"E57");var subQ7=sQuery(id+"F7.wireOp",EDGE,"E56");var subQ8=sQuery(id+"F5.wireOp",EDGE,"E54");var subQ9=sQuery(id+"F0.wireOp",EDGE,"E1");var subQ10=makeQuery(id+"F10.boolean.opBoolean","MERGE",EDGE,{"derivedFrom":[makeQuery(id+"F8.opExtrude","CAP_EDGE",EDGE,{"disambiguationData":[OSD([subQ7])],"isStart":true})],"fromTools":[makeQuery(id+"F10.opExtrude","SWEPT_EDGE",EDGE,{"disambiguationData":[OSD([subQ9,subQ4,subQ8,subQ3,subQ7,subQ6,subQ1,subQ5])]})]});Q8=makeQuery(id+"F13.boolean.opBoolean","SPLIT",EDGE,{"disambiguationData":[TD([makeQuery(id+"F13.opExtrude","SWEPT_FACE",FACE,{"disambiguationData":[OSD([subQ0])]})])],"derivedFrom":subQ10});}
            var Q9;
            {var subQ0=sQuery(id+"F11.wireOp",EDGE,"E82");var subQ1=sQuery(id+"F9.wireOp",EDGE,"E61");var subQ2=sQuery(id+"F5.wireOp",EDGE,"E55");var subQ3=sQuery(id+"F0.wireOp",EDGE,"E9");var subQ5=sQuery(id+"F9.wireOp",EDGE,"E64");var subQ6=sQuery(id+"F7.wireOp",EDGE,"E57");var subQ7=sQuery(id+"F7.wireOp",EDGE,"E56");var subQ8=sQuery(id+"F5.wireOp",EDGE,"E54");var subQ9=sQuery(id+"F0.wireOp",EDGE,"E1");var subQ10=makeQuery(id+"F10.boolean.opBoolean","MERGE",EDGE,{"derivedFrom":[makeQuery(id+"F8.opExtrude","CAP_EDGE",EDGE,{"disambiguationData":[OSD([subQ7])],"isStart":true})],"fromTools":[makeQuery(id+"F10.opExtrude","SWEPT_EDGE",EDGE,{"disambiguationData":[OSD([subQ9,subQ3,subQ8,subQ2,subQ7,subQ6,subQ1,subQ5])]})]});Q9=makeQuery(id+"F13.boolean.opBoolean","SPLIT",EDGE,{"disambiguationData":[TD([makeQuery(id+"F13.opExtrude","SWEPT_FACE",FACE,{"disambiguationData":[OSD([subQ0])]})])],"derivedFrom":subQ10});}
            var Q10;
            {var subQ0=sQuery(id+"F5.wireOp",EDGE,"E54");var subQ1=sQuery(id+"F0.wireOp",EDGE,"E9");var subQ2=sQuery(id+"F5.wireOp",EDGE,"E55");var subQ3=sQuery(id+"F0.wireOp",EDGE,"E1");var subQ4=sQuery(id+"F7.wireOp",EDGE,"E57");var subQ5=sQuery(id+"F9.wireOp",EDGE,"E64");var subQ6=sQuery(id+"F9.wireOp",EDGE,"E61");var subQ7=sQuery(id+"F7.wireOp",EDGE,"E56");var subQ8=makeQuery(id+"F10.boolean.opBoolean","MERGE",EDGE,{"derivedFrom":[makeQuery(id+"F8.opExtrude","CAP_EDGE",EDGE,{"disambiguationData":[OSD([subQ7])],"isStart":true})],"fromTools":[makeQuery(id+"F10.opExtrude","SWEPT_EDGE",EDGE,{"disambiguationData":[OSD([subQ3,subQ1,subQ0,subQ2,subQ7,subQ4,subQ6,subQ5])]})]});Q10=makeQuery(id+"F13.boolean.opBoolean","SPLIT",EDGE,{"disambiguationData":[TD([makeQuery(id+"F2.opExtrude","SWEPT_FACE",FACE,{"disambiguationData":[OSD([subQ3])]})])],"derivedFrom":subQ8});}
            var Q11;
            {var subQ0=sQuery(id+"F5.wireOp",EDGE,"E54");var subQ2=sQuery(id+"F9.wireOp",EDGE,"E62");var subQ4=sQuery(id+"F5.wireOp",EDGE,"E53");var subQ6=sQuery(id+"F0.wireOp",EDGE,"E1");var subQ7=makeQuery(id+"F2.opExtrude","SWEPT_FACE",FACE,{"disambiguationData":[OSD([subQ6])]});var subQ8=sQuery(id+"F0.wireOp",EDGE,"E0");Q11=makeQuery(id+"F16.boolean.opBoolean","SPLIT",EDGE,{"disambiguationData":[TD([subQ7])],"derivedFrom":makeQuery(id+"F15.boolean.opBoolean","SPLIT",EDGE,{"disambiguationData":[TD([subQ7])],"derivedFrom":makeQuery(id+"F10.boolean.opBoolean","COPY",EDGE,{"derivedFrom":makeQuery(id+"F10.opExtrude","SWEPT_EDGE",EDGE,{"disambiguationData":[OSD([subQ8,subQ6,subQ4,subQ0,subQ2,sQuery(id+"F9.wireOp",EDGE,"E64")])]})})})});}
            var Q12;
            {var subQ0=sQuery(id+"F5.wireOp",EDGE,"E53");var subQ2=sQuery(id+"F0.wireOp",EDGE,"E0");var subQ4=sQuery(id+"F9.wireOp",EDGE,"E62");var subQ6=sQuery(id+"F5.wireOp",EDGE,"E54");var subQ7=sQuery(id+"F0.wireOp",EDGE,"E1");Q12=makeQuery(id+"F16.boolean.opBoolean","SPLIT",EDGE,{"disambiguationData":[TD([makeQuery(id+"F12.boolean.opBoolean","COPY",FACE,{"derivedFrom":makeQuery(id+"F12.opExtrude","SWEPT_FACE",FACE,{"disambiguationData":[OSD([sQuery(id+"F4.wireOp",EDGE,"E33")])]})})])],"derivedFrom":makeQuery(id+"F15.boolean.opBoolean","SPLIT",EDGE,{"disambiguationData":[TD([makeQuery(id+"F2.opExtrude","SWEPT_FACE",FACE,{"disambiguationData":[OSD([subQ7])]})])],"derivedFrom":makeQuery(id+"F10.boolean.opBoolean","COPY",EDGE,{"derivedFrom":makeQuery(id+"F10.opExtrude","SWEPT_EDGE",EDGE,{"disambiguationData":[OSD([subQ2,subQ7,subQ0,subQ6,subQ4,sQuery(id+"F9.wireOp",EDGE,"E64")])]})})})});}
            var Q13;
            {var subQ0=sQuery(id+"F5.wireOp",EDGE,"E53");var subQ2=sQuery(id+"F9.wireOp",EDGE,"E62");var subQ4=sQuery(id+"F0.wireOp",EDGE,"E0");var subQ6=sQuery(id+"F5.wireOp",EDGE,"E54");var subQ7=sQuery(id+"F0.wireOp",EDGE,"E1");Q13=makeQuery(id+"F16.boolean.opBoolean","SPLIT",EDGE,{"disambiguationData":[TD([makeQuery(id+"F12.boolean.opBoolean","COPY",FACE,{"derivedFrom":makeQuery(id+"F12.opExtrude","SWEPT_FACE",FACE,{"disambiguationData":[OSD([sQuery(id+"F4.wireOp",EDGE,"E31")])]})})])],"derivedFrom":makeQuery(id+"F15.boolean.opBoolean","SPLIT",EDGE,{"disambiguationData":[TD([makeQuery(id+"F2.opExtrude","SWEPT_FACE",FACE,{"disambiguationData":[OSD([subQ7])]})])],"derivedFrom":makeQuery(id+"F10.boolean.opBoolean","COPY",EDGE,{"derivedFrom":makeQuery(id+"F10.opExtrude","SWEPT_EDGE",EDGE,{"disambiguationData":[OSD([subQ4,subQ7,subQ0,subQ6,subQ2,sQuery(id+"F9.wireOp",EDGE,"E64")])]})})})});}
            var Q14;
            {var subQ0=makeQuery(id+"F12.boolean.opBoolean","COPY",FACE,{"derivedFrom":makeQuery(id+"F12.opExtrude","SWEPT_FACE",FACE,{"disambiguationData":[OSD([sQuery(id+"F4.wireOp",EDGE,"E29")])]})});var subQ1=sQuery(id+"F5.wireOp",EDGE,"E53");var subQ3=sQuery(id+"F9.wireOp",EDGE,"E62");var subQ6=sQuery(id+"F0.wireOp",EDGE,"E0");var subQ9=sQuery(id+"F5.wireOp",EDGE,"E54");var subQ10=sQuery(id+"F0.wireOp",EDGE,"E1");Q14=makeQuery(id+"F16.boolean.opBoolean","SPLIT",EDGE,{"disambiguationData":[TD([subQ0])],"derivedFrom":makeQuery(id+"F15.boolean.opBoolean","SPLIT",EDGE,{"disambiguationData":[TD([makeQuery(id+"F2.opExtrude","SWEPT_FACE",FACE,{"disambiguationData":[OSD([subQ10])]})])],"derivedFrom":makeQuery(id+"F10.boolean.opBoolean","COPY",EDGE,{"derivedFrom":makeQuery(id+"F10.opExtrude","SWEPT_EDGE",EDGE,{"disambiguationData":[OSD([subQ6,subQ10,subQ1,subQ9,subQ3,sQuery(id+"F9.wireOp",EDGE,"E64")])]})})})});}
            var Q15;
            {var subQ0=sQuery(id+"F5.wireOp",EDGE,"E53");var subQ4=sQuery(id+"F9.wireOp",EDGE,"E62");var subQ6=sQuery(id+"F0.wireOp",EDGE,"E0");Q15=makeQuery(id+"F16.boolean.opBoolean","SPLIT",EDGE,{"disambiguationData":[TD([makeQuery(id+"F12.boolean.opBoolean","COPY",FACE,{"derivedFrom":makeQuery(id+"F12.opExtrude","SWEPT_FACE",FACE,{"disambiguationData":[OSD([sQuery(id+"F4.wireOp",EDGE,"E27")])]})})])],"derivedFrom":makeQuery(id+"F15.boolean.opBoolean","SPLIT",EDGE,{"disambiguationData":[TD([makeQuery(id+"F2.opExtrude","SWEPT_FACE",FACE,{"disambiguationData":[OSD([sQuery(id+"F0.wireOp",EDGE,"E3")])]})])],"derivedFrom":makeQuery(id+"F10.boolean.opBoolean","COPY",EDGE,{"derivedFrom":makeQuery(id+"F10.opExtrude","SWEPT_EDGE",EDGE,{"disambiguationData":[OSD([subQ6,sQuery(id+"F0.wireOp",EDGE,"E1"),subQ0,sQuery(id+"F5.wireOp",EDGE,"E54"),subQ4,sQuery(id+"F9.wireOp",EDGE,"E64")])]})})})});}
            var Q16;
            {var subQ0=sQuery(id+"F5.wireOp",EDGE,"E53");var subQ2=sQuery(id+"F9.wireOp",EDGE,"E62");var subQ4=sQuery(id+"F0.wireOp",EDGE,"E0");Q16=makeQuery(id+"F16.boolean.opBoolean","SPLIT",EDGE,{"disambiguationData":[TD([makeQuery(id+"F12.boolean.opBoolean","COPY",FACE,{"derivedFrom":makeQuery(id+"F12.opExtrude","SWEPT_FACE",FACE,{"disambiguationData":[OSD([sQuery(id+"F4.wireOp",EDGE,"E25")])]})})])],"derivedFrom":makeQuery(id+"F15.boolean.opBoolean","SPLIT",EDGE,{"disambiguationData":[TD([makeQuery(id+"F2.opExtrude","SWEPT_FACE",FACE,{"disambiguationData":[OSD([sQuery(id+"F0.wireOp",EDGE,"E3")])]})])],"derivedFrom":makeQuery(id+"F10.boolean.opBoolean","COPY",EDGE,{"derivedFrom":makeQuery(id+"F10.opExtrude","SWEPT_EDGE",EDGE,{"disambiguationData":[OSD([subQ4,sQuery(id+"F0.wireOp",EDGE,"E1"),subQ0,sQuery(id+"F5.wireOp",EDGE,"E54"),subQ2,sQuery(id+"F9.wireOp",EDGE,"E64")])]})})})});}
            var Q17;
            {var subQ0=sQuery(id+"F5.wireOp",EDGE,"E53");var subQ2=sQuery(id+"F0.wireOp",EDGE,"E0");var subQ4=sQuery(id+"F9.wireOp",EDGE,"E62");Q17=makeQuery(id+"F16.boolean.opBoolean","SPLIT",EDGE,{"disambiguationData":[TD([makeQuery(id+"F12.boolean.opBoolean","COPY",FACE,{"derivedFrom":makeQuery(id+"F12.opExtrude","SWEPT_FACE",FACE,{"disambiguationData":[OSD([sQuery(id+"F4.wireOp",EDGE,"E23")])]})})])],"derivedFrom":makeQuery(id+"F15.boolean.opBoolean","SPLIT",EDGE,{"disambiguationData":[TD([makeQuery(id+"F2.opExtrude","SWEPT_FACE",FACE,{"disambiguationData":[OSD([sQuery(id+"F0.wireOp",EDGE,"E3")])]})])],"derivedFrom":makeQuery(id+"F10.boolean.opBoolean","COPY",EDGE,{"derivedFrom":makeQuery(id+"F10.opExtrude","SWEPT_EDGE",EDGE,{"disambiguationData":[OSD([subQ2,sQuery(id+"F0.wireOp",EDGE,"E1"),subQ0,sQuery(id+"F5.wireOp",EDGE,"E54"),subQ4,sQuery(id+"F9.wireOp",EDGE,"E64")])]})})})});}
            var Q18;
            {var subQ0=sQuery(id+"F0.wireOp",EDGE,"E0");var subQ2=sQuery(id+"F9.wireOp",EDGE,"E62");var subQ4=sQuery(id+"F5.wireOp",EDGE,"E53");Q18=makeQuery(id+"F16.boolean.opBoolean","SPLIT",EDGE,{"disambiguationData":[TD([makeQuery(id+"F12.boolean.opBoolean","COPY",FACE,{"derivedFrom":makeQuery(id+"F12.opExtrude","SWEPT_FACE",FACE,{"disambiguationData":[OSD([sQuery(id+"F4.wireOp",EDGE,"E21")])]})})])],"derivedFrom":makeQuery(id+"F15.boolean.opBoolean","SPLIT",EDGE,{"disambiguationData":[TD([makeQuery(id+"F2.opExtrude","SWEPT_FACE",FACE,{"disambiguationData":[OSD([sQuery(id+"F0.wireOp",EDGE,"E3")])]})])],"derivedFrom":makeQuery(id+"F10.boolean.opBoolean","COPY",EDGE,{"derivedFrom":makeQuery(id+"F10.opExtrude","SWEPT_EDGE",EDGE,{"disambiguationData":[OSD([subQ0,sQuery(id+"F0.wireOp",EDGE,"E1"),subQ4,sQuery(id+"F5.wireOp",EDGE,"E54"),subQ2,sQuery(id+"F9.wireOp",EDGE,"E64")])]})})})});}
            var Q19;
            {var subQ0=sQuery(id+"F9.wireOp",EDGE,"E62");var subQ2=sQuery(id+"F0.wireOp",EDGE,"E0");var subQ4=sQuery(id+"F5.wireOp",EDGE,"E53");Q19=makeQuery(id+"F16.boolean.opBoolean","SPLIT",EDGE,{"disambiguationData":[TD([makeQuery(id+"F12.boolean.opBoolean","COPY",FACE,{"derivedFrom":makeQuery(id+"F12.opExtrude","SWEPT_FACE",FACE,{"disambiguationData":[OSD([sQuery(id+"F4.wireOp",EDGE,"E16")])]})})])],"derivedFrom":makeQuery(id+"F15.boolean.opBoolean","SPLIT",EDGE,{"disambiguationData":[TD([makeQuery(id+"F2.opExtrude","SWEPT_FACE",FACE,{"disambiguationData":[OSD([sQuery(id+"F0.wireOp",EDGE,"E3")])]})])],"derivedFrom":makeQuery(id+"F10.boolean.opBoolean","COPY",EDGE,{"derivedFrom":makeQuery(id+"F10.opExtrude","SWEPT_EDGE",EDGE,{"disambiguationData":[OSD([subQ2,sQuery(id+"F0.wireOp",EDGE,"E1"),subQ4,sQuery(id+"F5.wireOp",EDGE,"E54"),subQ0,sQuery(id+"F9.wireOp",EDGE,"E64")])]})})})});}
            var Q20;
            {var subQ0=sQuery(id+"F0.wireOp",EDGE,"E0");var subQ2=sQuery(id+"F9.wireOp",EDGE,"E62");var subQ4=sQuery(id+"F5.wireOp",EDGE,"E53");Q20=makeQuery(id+"F16.boolean.opBoolean","SPLIT",EDGE,{"disambiguationData":[TD([makeQuery(id+"F12.boolean.opBoolean","COPY",FACE,{"derivedFrom":makeQuery(id+"F12.opExtrude","SWEPT_FACE",FACE,{"disambiguationData":[OSD([sQuery(id+"F4.wireOp",EDGE,"E13")])]})})])],"derivedFrom":makeQuery(id+"F15.boolean.opBoolean","SPLIT",EDGE,{"disambiguationData":[TD([makeQuery(id+"F2.opExtrude","SWEPT_FACE",FACE,{"disambiguationData":[OSD([sQuery(id+"F0.wireOp",EDGE,"E3")])]})])],"derivedFrom":makeQuery(id+"F10.boolean.opBoolean","COPY",EDGE,{"derivedFrom":makeQuery(id+"F10.opExtrude","SWEPT_EDGE",EDGE,{"disambiguationData":[OSD([subQ0,sQuery(id+"F0.wireOp",EDGE,"E1"),subQ4,sQuery(id+"F5.wireOp",EDGE,"E54"),subQ2,sQuery(id+"F9.wireOp",EDGE,"E64")])]})})})});}
            var Q21;
            {var subQ0=sQuery(id+"F5.wireOp",EDGE,"E53");var subQ2=makeQuery(id+"F2.opExtrude","SWEPT_FACE",FACE,{"disambiguationData":[OSD([sQuery(id+"F0.wireOp",EDGE,"E3")])]});var subQ4=sQuery(id+"F0.wireOp",EDGE,"E0");var subQ7=sQuery(id+"F9.wireOp",EDGE,"E62");Q21=makeQuery(id+"F16.boolean.opBoolean","SPLIT",EDGE,{"disambiguationData":[TD([subQ2])],"derivedFrom":makeQuery(id+"F15.boolean.opBoolean","SPLIT",EDGE,{"disambiguationData":[TD([subQ2])],"derivedFrom":makeQuery(id+"F10.boolean.opBoolean","COPY",EDGE,{"derivedFrom":makeQuery(id+"F10.opExtrude","SWEPT_EDGE",EDGE,{"disambiguationData":[OSD([subQ4,sQuery(id+"F0.wireOp",EDGE,"E1"),subQ0,sQuery(id+"F5.wireOp",EDGE,"E54"),subQ7,sQuery(id+"F9.wireOp",EDGE,"E64")])]})})})});}
            var Q22;
            {var subQ0=sQuery(id+"F7.wireOp",EDGE,"E58");var subQ1=sQuery(id+"F5.wireOp",EDGE,"E54");var subQ3=sQuery(id+"F9.wireOp",EDGE,"E62");Q22=makeQuery(id+"F13.boolean.opBoolean","SPLIT",EDGE,{"disambiguationData":[TD([makeQuery(id+"F2.opExtrude","SWEPT_FACE",FACE,{"disambiguationData":[OSD([sQuery(id+"F0.wireOp",EDGE,"E3")])]})])],"derivedFrom":makeQuery(id+"F10.boolean.opBoolean","COPY",EDGE,{"derivedFrom":makeQuery(id+"F10.opExtrude","SWEPT_EDGE",EDGE,{"disambiguationData":[OSD([subQ1,sQuery(id+"F7.wireOp",EDGE,"E57"),subQ0,subQ3,sQuery(id+"F9.wireOp",EDGE,"E63")])]})})});}
            var Q23;
            {var subQ0=sQuery(id+"F9.wireOp",EDGE,"E62");var subQ1=sQuery(id+"F7.wireOp",EDGE,"E58");var subQ2=sQuery(id+"F5.wireOp",EDGE,"E54");Q23=makeQuery(id+"F13.boolean.opBoolean","SPLIT",EDGE,{"disambiguationData":[TD([makeQuery(id+"F13.opExtrude","SWEPT_FACE",FACE,{"disambiguationData":[OSD([sQuery(id+"F11.wireOp",EDGE,"E66")])]})])],"derivedFrom":makeQuery(id+"F10.boolean.opBoolean","COPY",EDGE,{"derivedFrom":makeQuery(id+"F10.opExtrude","SWEPT_EDGE",EDGE,{"disambiguationData":[OSD([subQ2,sQuery(id+"F7.wireOp",EDGE,"E57"),subQ1,subQ0,sQuery(id+"F9.wireOp",EDGE,"E63")])]})})});}
            var Q24;
            {var subQ0=sQuery(id+"F9.wireOp",EDGE,"E62");var subQ1=sQuery(id+"F7.wireOp",EDGE,"E58");var subQ2=sQuery(id+"F5.wireOp",EDGE,"E54");Q24=makeQuery(id+"F13.boolean.opBoolean","SPLIT",EDGE,{"disambiguationData":[TD([makeQuery(id+"F13.opExtrude","SWEPT_FACE",FACE,{"disambiguationData":[OSD([sQuery(id+"F11.wireOp",EDGE,"E68")])]})])],"derivedFrom":makeQuery(id+"F10.boolean.opBoolean","COPY",EDGE,{"derivedFrom":makeQuery(id+"F10.opExtrude","SWEPT_EDGE",EDGE,{"disambiguationData":[OSD([subQ2,sQuery(id+"F7.wireOp",EDGE,"E57"),subQ1,subQ0,sQuery(id+"F9.wireOp",EDGE,"E63")])]})})});}
            var Q25;
            {var subQ0=sQuery(id+"F9.wireOp",EDGE,"E62");var subQ1=sQuery(id+"F7.wireOp",EDGE,"E58");var subQ2=sQuery(id+"F5.wireOp",EDGE,"E54");Q25=makeQuery(id+"F13.boolean.opBoolean","SPLIT",EDGE,{"disambiguationData":[TD([makeQuery(id+"F13.opExtrude","SWEPT_FACE",FACE,{"disambiguationData":[OSD([sQuery(id+"F11.wireOp",EDGE,"E70")])]})])],"derivedFrom":makeQuery(id+"F10.boolean.opBoolean","COPY",EDGE,{"derivedFrom":makeQuery(id+"F10.opExtrude","SWEPT_EDGE",EDGE,{"disambiguationData":[OSD([subQ2,sQuery(id+"F7.wireOp",EDGE,"E57"),subQ1,subQ0,sQuery(id+"F9.wireOp",EDGE,"E63")])]})})});}
            var Q26;
            {var subQ0=sQuery(id+"F9.wireOp",EDGE,"E62");var subQ1=sQuery(id+"F7.wireOp",EDGE,"E58");var subQ2=sQuery(id+"F5.wireOp",EDGE,"E54");Q26=makeQuery(id+"F13.boolean.opBoolean","SPLIT",EDGE,{"disambiguationData":[TD([makeQuery(id+"F13.opExtrude","SWEPT_FACE",FACE,{"disambiguationData":[OSD([sQuery(id+"F11.wireOp",EDGE,"E72")])]})])],"derivedFrom":makeQuery(id+"F10.boolean.opBoolean","COPY",EDGE,{"derivedFrom":makeQuery(id+"F10.opExtrude","SWEPT_EDGE",EDGE,{"disambiguationData":[OSD([subQ2,sQuery(id+"F7.wireOp",EDGE,"E57"),subQ1,subQ0,sQuery(id+"F9.wireOp",EDGE,"E63")])]})})});}
            var Q27;
            {var subQ0=sQuery(id+"F9.wireOp",EDGE,"E62");var subQ1=sQuery(id+"F7.wireOp",EDGE,"E58");var subQ2=sQuery(id+"F5.wireOp",EDGE,"E54");Q27=makeQuery(id+"F13.boolean.opBoolean","SPLIT",EDGE,{"disambiguationData":[TD([makeQuery(id+"F13.opExtrude","SWEPT_FACE",FACE,{"disambiguationData":[OSD([sQuery(id+"F11.wireOp",EDGE,"E74")])]})])],"derivedFrom":makeQuery(id+"F10.boolean.opBoolean","COPY",EDGE,{"derivedFrom":makeQuery(id+"F10.opExtrude","SWEPT_EDGE",EDGE,{"disambiguationData":[OSD([subQ2,sQuery(id+"F7.wireOp",EDGE,"E57"),subQ1,subQ0,sQuery(id+"F9.wireOp",EDGE,"E63")])]})})});}
            var Q28;
            {var subQ0=sQuery(id+"F9.wireOp",EDGE,"E62");var subQ1=sQuery(id+"F7.wireOp",EDGE,"E58");var subQ2=sQuery(id+"F5.wireOp",EDGE,"E54");Q28=makeQuery(id+"F13.boolean.opBoolean","SPLIT",EDGE,{"disambiguationData":[TD([makeQuery(id+"F13.opExtrude","SWEPT_FACE",FACE,{"disambiguationData":[OSD([sQuery(id+"F11.wireOp",EDGE,"E76")])]})])],"derivedFrom":makeQuery(id+"F10.boolean.opBoolean","COPY",EDGE,{"derivedFrom":makeQuery(id+"F10.opExtrude","SWEPT_EDGE",EDGE,{"disambiguationData":[OSD([subQ2,sQuery(id+"F7.wireOp",EDGE,"E57"),subQ1,subQ0,sQuery(id+"F9.wireOp",EDGE,"E63")])]})})});}
            var Q29;
            {var subQ0=sQuery(id+"F7.wireOp",EDGE,"E58");var subQ1=sQuery(id+"F9.wireOp",EDGE,"E62");var subQ2=sQuery(id+"F5.wireOp",EDGE,"E54");Q29=makeQuery(id+"F13.boolean.opBoolean","SPLIT",EDGE,{"disambiguationData":[TD([makeQuery(id+"F13.opExtrude","SWEPT_FACE",FACE,{"disambiguationData":[OSD([sQuery(id+"F11.wireOp",EDGE,"E78")])]})])],"derivedFrom":makeQuery(id+"F10.boolean.opBoolean","COPY",EDGE,{"derivedFrom":makeQuery(id+"F10.opExtrude","SWEPT_EDGE",EDGE,{"disambiguationData":[OSD([subQ2,sQuery(id+"F7.wireOp",EDGE,"E57"),subQ0,subQ1,sQuery(id+"F9.wireOp",EDGE,"E63")])]})})});}
            var Q30;
            {var subQ0=sQuery(id+"F9.wireOp",EDGE,"E62");var subQ1=sQuery(id+"F5.wireOp",EDGE,"E54");var subQ2=sQuery(id+"F7.wireOp",EDGE,"E58");Q30=makeQuery(id+"F13.boolean.opBoolean","SPLIT",EDGE,{"disambiguationData":[TD([makeQuery(id+"F13.opExtrude","SWEPT_FACE",FACE,{"disambiguationData":[OSD([sQuery(id+"F11.wireOp",EDGE,"E80")])]})])],"derivedFrom":makeQuery(id+"F10.boolean.opBoolean","COPY",EDGE,{"derivedFrom":makeQuery(id+"F10.opExtrude","SWEPT_EDGE",EDGE,{"disambiguationData":[OSD([subQ1,sQuery(id+"F7.wireOp",EDGE,"E57"),subQ2,subQ0,sQuery(id+"F9.wireOp",EDGE,"E63")])]})})});}
            var Q31;
            {var subQ0=sQuery(id+"F9.wireOp",EDGE,"E62");var subQ1=sQuery(id+"F7.wireOp",EDGE,"E58");var subQ2=sQuery(id+"F5.wireOp",EDGE,"E54");Q31=makeQuery(id+"F13.boolean.opBoolean","SPLIT",EDGE,{"disambiguationData":[TD([makeQuery(id+"F13.opExtrude","SWEPT_FACE",FACE,{"disambiguationData":[OSD([sQuery(id+"F11.wireOp",EDGE,"E82")])]})])],"derivedFrom":makeQuery(id+"F10.boolean.opBoolean","COPY",EDGE,{"derivedFrom":makeQuery(id+"F10.opExtrude","SWEPT_EDGE",EDGE,{"disambiguationData":[OSD([subQ2,sQuery(id+"F7.wireOp",EDGE,"E57"),subQ1,subQ0,sQuery(id+"F9.wireOp",EDGE,"E63")])]})})});}
            var Q32;
            {var subQ0=sQuery(id+"F5.wireOp",EDGE,"E54");var subQ1=sQuery(id+"F9.wireOp",EDGE,"E62");var subQ2=sQuery(id+"F7.wireOp",EDGE,"E57");var subQ3=sQuery(id+"F7.wireOp",EDGE,"E58");Q32=makeQuery(id+"F13.boolean.opBoolean","SPLIT",EDGE,{"disambiguationData":[TD([makeQuery(id+"F2.opExtrude","SWEPT_FACE",FACE,{"disambiguationData":[OSD([sQuery(id+"F0.wireOp",EDGE,"E1")])]})])],"derivedFrom":makeQuery(id+"F10.boolean.opBoolean","COPY",EDGE,{"derivedFrom":makeQuery(id+"F10.opExtrude","SWEPT_EDGE",EDGE,{"disambiguationData":[OSD([subQ0,subQ2,subQ3,subQ1,sQuery(id+"F9.wireOp",EDGE,"E63")])]})})});}
            fillet(context, id + "F19", {"entities" : qUnion([Q0, Q1, Q2, Q3, Q4, Q5, Q6, Q7, Q8, Q9, Q10, Q11, Q12, Q13, Q14, Q15, Q16, Q17, Q18, Q19, Q20, Q21, Q22, Q23, Q24, Q25, Q26, Q27, Q28, Q29, Q30, Q31, Q32]), "radius" : 5 * mm, "tangentPropagation" : true, "allowEdgeOverflow" : false});
        }
        {
            var Q0;
            Q0=makeQuery(id+"F1.opExtrude","CAP_EDGE",EDGE,{"disambiguationData":[OSD([sQuery(id+"F0.wireOp",EDGE,"E2")])],"isStart":false});
            var Q1;
            Q1=makeQuery(id+"F1.opExtrude","CAP_EDGE",EDGE,{"disambiguationData":[OSD([sQuery(id+"F0.wireOp",EDGE,"E1")])],"isStart":false});
            var Q2;
            Q2=makeQuery(id+"F1.opExtrude","CAP_EDGE",EDGE,{"disambiguationData":[OSD([sQuery(id+"F0.wireOp",EDGE,"E3")])],"isStart":false});
            fillet(context, id + "F20", {"entities" : qUnion([Q0, Q1, Q2]), "radius" : 5 * mm, "tangentPropagation" : true, "allowEdgeOverflow" : false});
        }
    });
